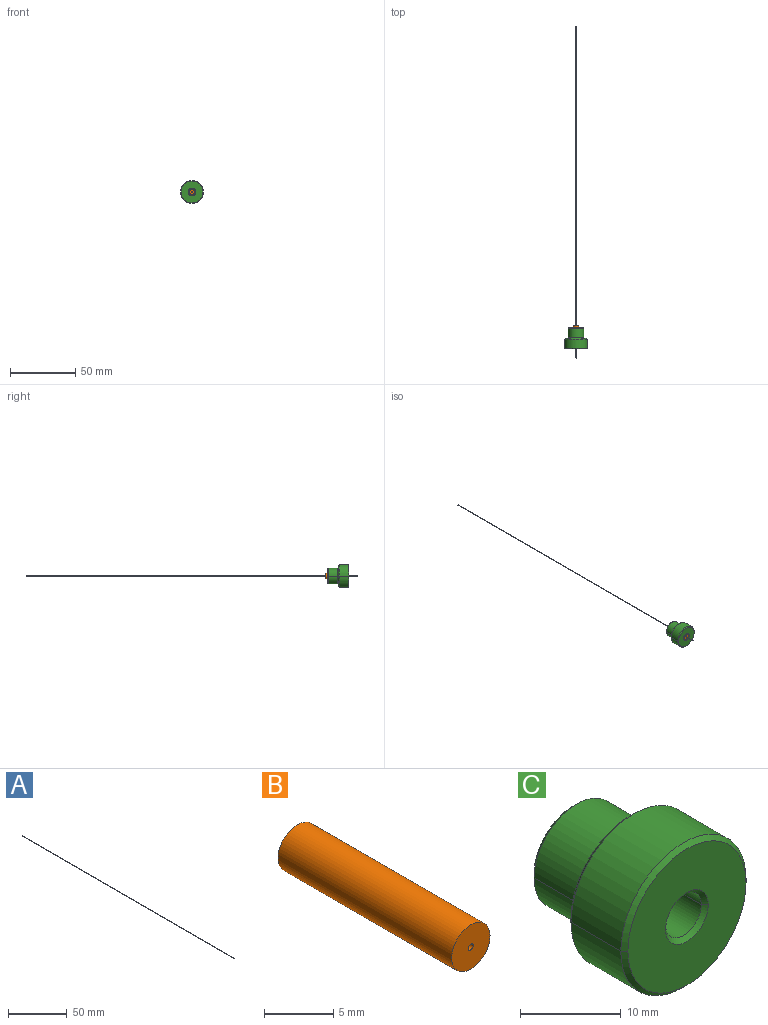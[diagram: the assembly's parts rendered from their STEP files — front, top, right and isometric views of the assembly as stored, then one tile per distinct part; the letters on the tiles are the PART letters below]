
ASSEMBLY  parts=3 mates=3
PART A: 3 faces, bbox 0.4x254x0.4 mm
  f0: cylinder r=0.19mm len=254mm, axis (0,1,0), area 307.2mm2, adj f1,f2
  f1: plane 0.39x0.39mm, normal (0,-1,0), area 0.1mm2, adj f0
  f2: plane 0.39x0.39mm, normal (0,1,0), area 0.1mm2, adj f0
PART B: 4 faces, bbox 3.9x17.8x3.9 mm
  f0: cylinder r=1.97mm len=17.78mm, axis (0,1,0), area 220mm2, adj f1,f2
  f1: plane 3.94x3.94mm, normal (0,-1,0), area 12mm2, adj f0,f3
  f2: plane 3.94x3.94mm, normal (0,1,0), area 12mm2, adj f0,f3
  f3: cylinder r=0.25mm len=17.78mm, axis (0,1,0), area 28.4mm2, adj f1,f2
PART C: 21 faces, bbox 17.6x16x17.6 mm
  f0: plane 16.6x16.6mm, normal (0,-1,0), area 188.1mm2, adj f1,f2,f19,f20
  f1: cone r=8.8mm half-angle=45deg, axis (0,1,0), area 19mm2, adj f0,f2,f4
  f2: cone r=8.8mm half-angle=45deg, axis (0,1,0), area 19mm2, adj f0,f1,f3
  f3: cylinder r=8.8mm len=17.6mm, axis (0,-1,0), area 193.5mm2, adj f2,f4,f6
  f4: cylinder r=8.8mm len=17.6mm, axis (0,-1,0), area 193.5mm2, adj f1,f3,f5
  f5: cone r=8.3mm half-angle=45deg, axis (0,-1,0), area 19mm2, adj f4,f6,f7
  f6: cone r=8.3mm half-angle=45deg, axis (0,-1,0), area 19mm2, adj f3,f5,f7
  f7: plane 16.6x16.6mm, normal (0,1,0), area 83.7mm2, adj f5,f6,f8,f9
  f8: torus R=6.5mm, axis (0,1,0), area 15.3mm2, adj f7,f9,f11
  f9: torus R=6.5mm, axis (0,1,0), area 15.3mm2, adj f7,f8,f10
  f10: cylinder r=6mm len=12mm, axis (0,-1,0), area 131.9mm2, adj f9,f11,f13
  f11: cylinder r=6mm len=12mm, axis (0,-1,0), area 131.9mm2, adj f8,f10,f12
  f12: cone r=5.5mm half-angle=45deg, axis (0,-1,0), area 12.8mm2, adj f11,f13,f14
  f13: cone r=5.5mm half-angle=45deg, axis (0,-1,0), area 12.8mm2, adj f10,f12,f14
  f14: plane 11x11mm, normal (0,1,0), area 66.8mm2, adj f12,f13,f15,f16
  f15: cone r=2.5mm half-angle=45deg, axis (0,1,0), area 6.1mm2, adj f14,f16,f18
  f16: cone r=2.5mm half-angle=45deg, axis (0,1,0), area 6.1mm2, adj f14,f15,f17
  f17: cylinder r=2.5mm len=15mm, axis (0,-1,0), area 117.8mm2, adj f16,f18,f20
  f18: cylinder r=2.5mm len=15mm, axis (0,-1,0), area 117.8mm2, adj f15,f17,f19
  f19: cone r=3mm half-angle=45deg, axis (0,-1,0), area 6.1mm2, adj f0,f18,f20
  f20: cone r=3mm half-angle=45deg, axis (0,-1,0), area 6.1mm2, adj f0,f17,f19
PLACE A t=(-348.09,200.88,-86.84)mm
PLACE B t=(-348.09,-28.34,-86.84)mm
PLACE C t=(-348.09,-46.12,-86.84)mm
MATE slider A.f0 <-> B.f3  axis (0,1,0) through (-348.09,73.88,-86.84)mm
MATE slider B.f0 <-> C.f1  axis (0,1,0) through (-348.09,-37.23,-86.84)mm
MATE planar C.f1 <-> B.f0  axis (0,-1,0) through (-348.09,-46.12,-86.84)mm
